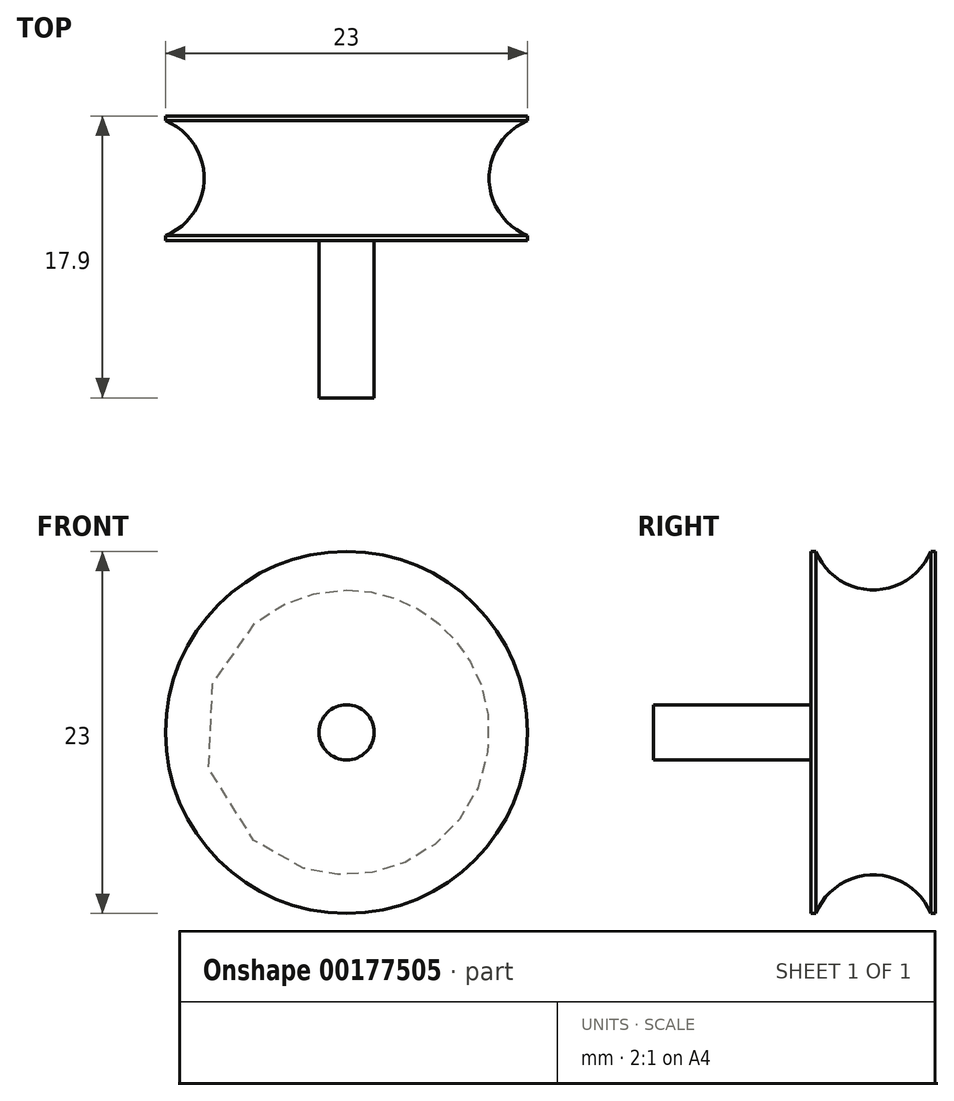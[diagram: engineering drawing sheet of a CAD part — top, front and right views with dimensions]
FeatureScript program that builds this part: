
annotation { "Feature Type Name" : "Feature", "Feature Type Description" : "" }
export const myFeature = defineFeature(function(context is Context, id is Id, definition is map)
    precondition{}
    {
        {
            var Q0;
            Q0=qCreatedBy(makeId("Front.planeOp"),FACE);
            var sketch = newSketch(context, id + "F0", { "sketchPlane" : qUnion([Q0])});
            skCircle(sketch, "E0", {"center": v(0, 0) * mm, "radius": 11.5 * mm});
            skSolve(sketch);
        }
        {
            var Q0;
            Q0 = qSketchRegion(id + "F0", true);
            extrude(context, id + "F1", {"entities" : qUnion([Q0]), "depth" : 7.9 * mm});
        }
        {
            var Q0;
            Q0=makeQuery(id+"F1.opExtrude","CAP_FACE",FACE,{"disambiguationData":[OSD([sQuery(id+"F0.wireOp",EDGE,"E0")])],"isStart":false});
            var sketch = newSketch(context, id + "F2", { "sketchPlane" : qUnion([Q0])});
            skCircle(sketch, "E1", {"center": v(0, 0) * mm, "radius": 1.75 * mm});
            skSolve(sketch);
        }
        {
            var Q0;
            Q0 = qSketchRegion(id + "F2", true);
            extrude(context, id + "F3", {"entities" : qUnion([Q0]), "operationType" : NewBodyOperationType.ADD, "depth" : 10 * mm});
        }
        {
            var Q0;
            Q0=qCreatedBy(makeId("Right.planeOp"),FACE);
            var sketch = newSketch(context, id + "F4", { "sketchPlane" : qUnion([Q0])});
            skCircle(sketch, "E2", {"center": v(-3.95, 13) * mm, "radius": 3.95 * mm});
            skLineSegment(sketch, "E3", {"start": v(-7.21, 0) * mm, "end": v(-3.09, 0) * mm});
            skSolve(sketch);
        }
        {
            var Q0;
            Q0=makeQuery(id+"F4.imprint","IMPRINT",FACE,{"disambiguationData":[TD([[makeQuery(id+"F4.imprint","IMPRINT",EDGE,{"derivedFrom":sQuery(id+"F4.wireOp",EDGE,"E2")}),1.0]])]});
            var Q1;
            Q1=sQuery(id+"F4.wireOp",EDGE,"E3");
            revolve(context, id + "F5", {"operationType" : NewBodyOperationType.REMOVE, "entities" : qUnion([Q0]), "axis" : qUnion([Q1]), "revolveType" : RevolveType.FULL, "oppositeDirection" : true});
        }
    });
